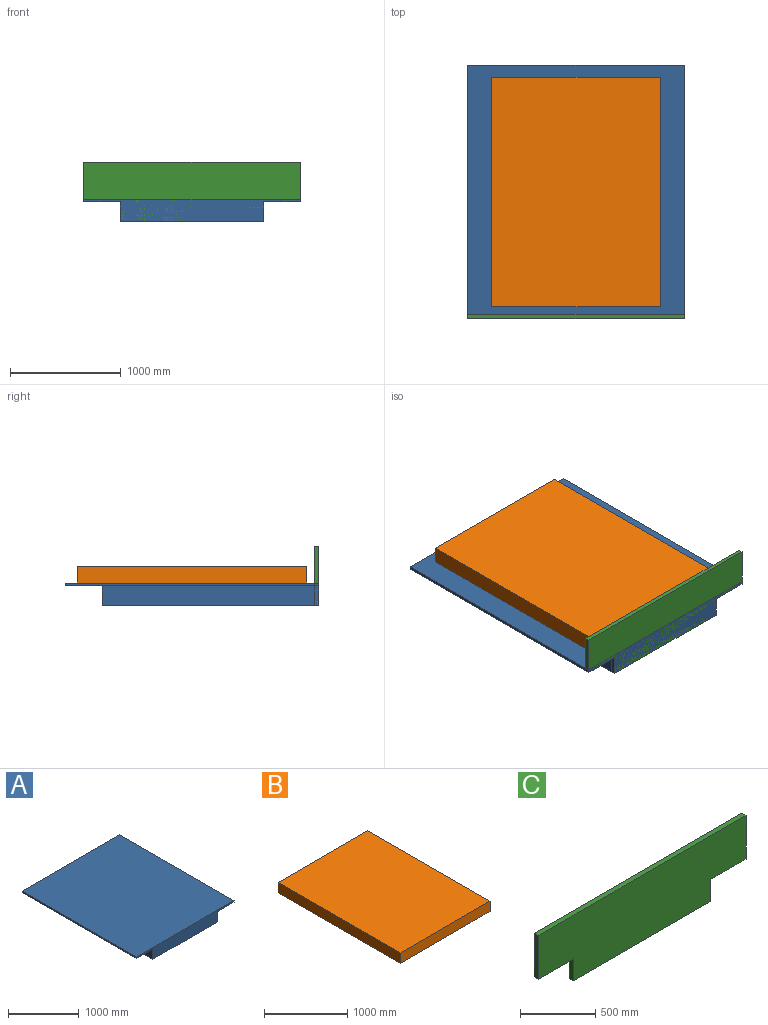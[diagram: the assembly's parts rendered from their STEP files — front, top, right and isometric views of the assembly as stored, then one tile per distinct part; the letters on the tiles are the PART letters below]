
ASSEMBLY  parts=3 mates=2
PART A: 10 faces, bbox 1955.8x2286x203.2 mm
  f0: plane 1955.8x25.4mm, normal (0,1,0), area 49677.3mm2, adj f1,f3,f4,f5
  f1: plane 2286x25.4mm, normal (-1,0,0), area 58064.4mm2, adj f0,f2,f4,f5
  f2: plane 1955.8x203.2mm, normal (0,-1,0), area 279999.4mm2, adj f1,f3,f4,f5,f7,f8,f9
  f3: plane 2286x25.4mm, normal (1,0,0), area 58064.4mm2, adj f0,f2,f4,f5
  f4: plane 2286x1955.8mm, normal (0,0,-1), area 1937415.4mm2, adj f0,f1,f2,f3,f6,f7,f8
  f5: plane 2286x1955.8mm, normal (0,0,1), area 4470958.8mm2, adj f0,f1,f2,f3
  f6: plane 1295.4x177.8mm, normal (0,1,0), area 230322.1mm2, adj f4,f7,f8,f9
  f7: plane 1955.8x177.8mm, normal (1,0,0), area 347741.2mm2, adj f2,f4,f6,f9
  f8: plane 1955.8x177.8mm, normal (-1,0,0), area 347741.2mm2, adj f2,f4,f6,f9
  f9: plane 1955.8x1295.4mm, normal (0,0,-1), area 2533543.4mm2, adj f2,f6,f7,f8
PART B: 6 faces, bbox 1524x2070.1x152.4 mm
  f0: plane 1524x152.4mm, normal (0,1,0), area 232257.6mm2, adj f1,f3,f4,f5
  f1: plane 2070.1x152.4mm, normal (-1,0,0), area 315483.2mm2, adj f0,f2,f4,f5
  f2: plane 1524x152.4mm, normal (0,-1,0), area 232257.6mm2, adj f1,f3,f4,f5
  f3: plane 2070.1x152.4mm, normal (1,0,0), area 315483.2mm2, adj f0,f2,f4,f5
  f4: plane 2070.1x1524mm, normal (0,0,1), area 3154832.4mm2, adj f0,f1,f2,f3
  f5: plane 2070.1x1524mm, normal (0,0,-1), area 3154832.4mm2, adj f0,f1,f2,f3
PART C: 10 faces, bbox 1955.8x38.1x533.4 mm
  f0: plane 355.6x38.1mm, normal (-1,0,0), area 13548.4mm2, adj f1,f7,f8,f9
  f1: plane 330.2x38.1mm, normal (0,0,-1), area 12580.6mm2, adj f0,f2,f8,f9
  f2: plane 177.8x38.1mm, normal (-1,0,0), area 6774.2mm2, adj f1,f3,f8,f9
  f3: plane 1295.4x38.1mm, normal (0,0,-1), area 49354.7mm2, adj f2,f4,f8,f9
  f4: plane 177.8x38.1mm, normal (1,0,0), area 6774.2mm2, adj f3,f5,f8,f9
  f5: plane 330.2x38.1mm, normal (0,0,-1), area 12580.6mm2, adj f4,f6,f8,f9
  f6: plane 355.6x38.1mm, normal (1,0,0), area 13548.4mm2, adj f5,f7,f8,f9
  f7: plane 1955.8x38.1mm, normal (0,0,1), area 74516mm2, adj f0,f6,f8,f9
  f8: plane 1955.8x533.4mm, normal (0,-1,0), area 925804.6mm2, adj f0,f1,f2,f3,f4,f5,f6,f7
  f9: plane 1955.8x533.4mm, normal (0,1,0), area 925804.6mm2, adj f0,f1,f2,f3,f4,f5,f6,f7
PLACE A t=(125.77,219.2,-265.19)mm
PLACE B rot(axis=(1,0,0),180deg) t=(125.77,111.25,-112.79)mm
PLACE C t=(125.77,257.3,-265.19)mm
MATE fastened B.f4 <-> A.f5  axis (0,0,-1) through (125.77,219.2,-265.19)mm
MATE fastened C.f8 <-> A.f2  axis (0,-1,0) through (125.77,-923.8,-468.39)mm
